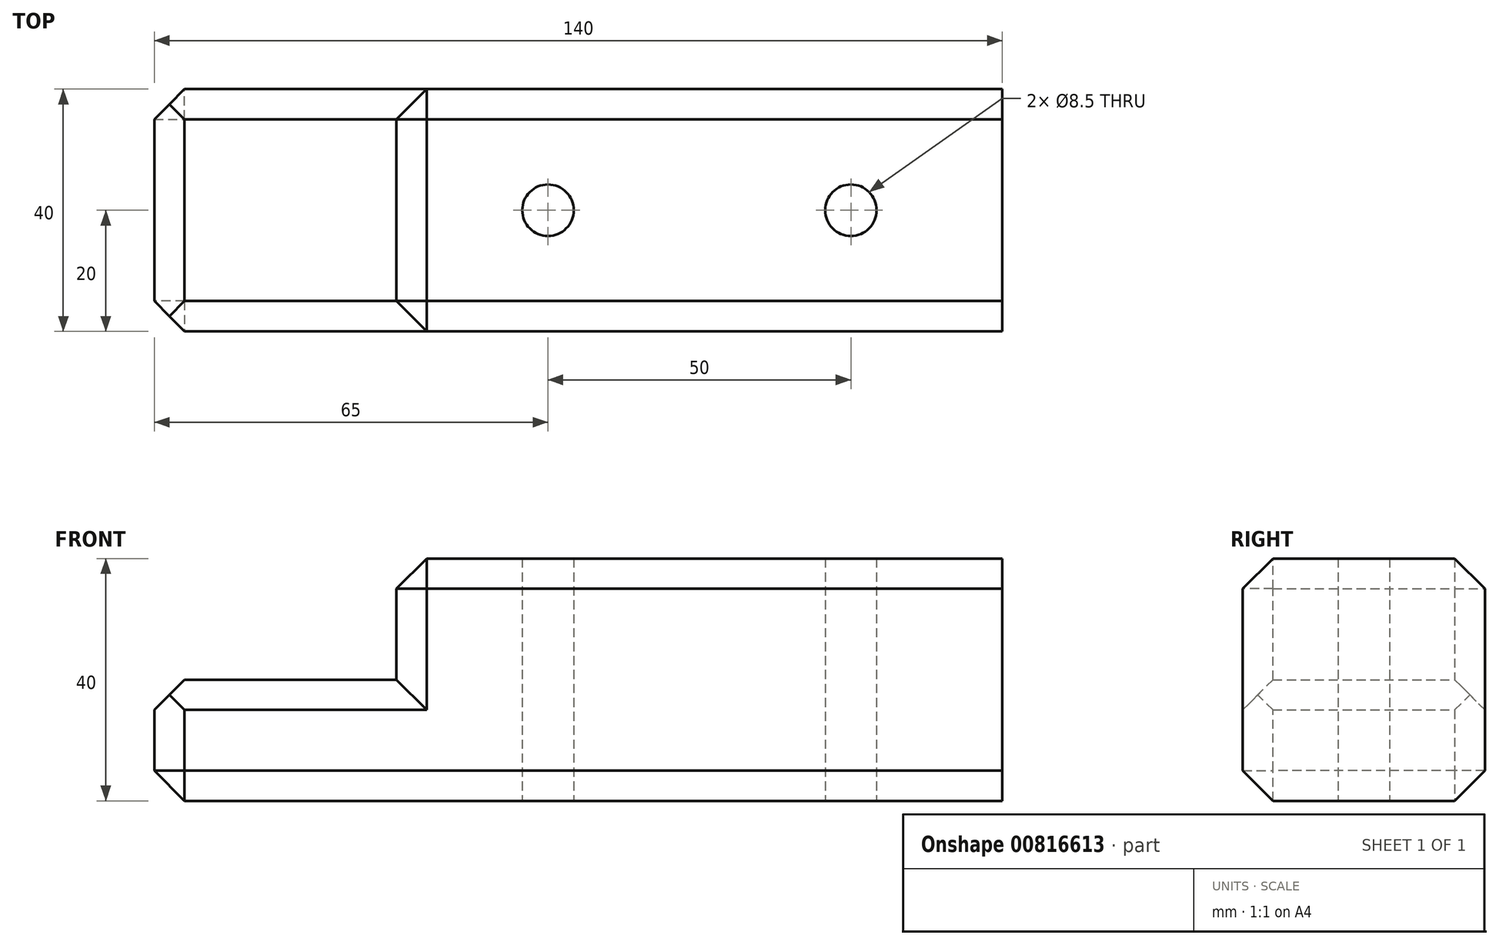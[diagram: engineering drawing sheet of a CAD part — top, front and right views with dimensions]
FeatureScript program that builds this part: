
annotation { "Feature Type Name" : "Feature", "Feature Type Description" : "" }
export const myFeature = defineFeature(function(context is Context, id is Id, definition is map)
    precondition{}
    {
        {
            var Q0;
            Q0=qCreatedBy(makeId("Front.planeOp"),FACE);
            var sketch = newSketch(context, id + "F0", { "sketchPlane" : qUnion([Q0])});
            skLineSegment(sketch, "E0", {"start": v(0, 0) * mm, "end": v(140, 0) * mm});
            skLineSegment(sketch, "E1", {"start": v(140, 0) * mm, "end": v(140, 40) * mm});
            skLineSegment(sketch, "E2", {"start": v(140, 40) * mm, "end": v(40, 40) * mm});
            skLineSegment(sketch, "E3", {"start": v(40, 40) * mm, "end": v(40, 20) * mm});
            skLineSegment(sketch, "E4", {"start": v(40, 20) * mm, "end": v(0, 20) * mm});
            skLineSegment(sketch, "E5", {"start": v(0, 20) * mm, "end": v(0, 0) * mm});
            skSolve(sketch);
        }
        {
            var Q0;
            Q0=makeQuery(id+"F0.imprint","IMPRINT",FACE,{"disambiguationData":[TD([[makeQuery(id+"F0.imprint","IMPRINT",EDGE,{"derivedFrom":sQuery(id+"F0.wireOp",EDGE,"E0")}),1.0]])]});
            extrude(context, id + "F1", {"entities" : qUnion([Q0]), "depth" : 40 * mm, "offsetDistance" : 25 * mm});
        }
        {
            var Q0;
            Q0=makeQuery(id+"F1.opExtrude","SWEPT_EDGE",EDGE,{"disambiguationData":[OSD([sQuery(id+"F0.wireOp",EDGE,"E2"),sQuery(id+"F0.wireOp",EDGE,"E3")])]});
            var Q1;
            Q1=makeQuery(id+"F1.opExtrude","CAP_EDGE",EDGE,{"disambiguationData":[OSD([sQuery(id+"F0.wireOp",EDGE,"E3")])],"isStart":false});
            var Q2;
            Q2=makeQuery(id+"F1.opExtrude","CAP_EDGE",EDGE,{"disambiguationData":[OSD([sQuery(id+"F0.wireOp",EDGE,"E3")])],"isStart":true});
            var Q3;
            Q3=makeQuery(id+"F1.opExtrude","SWEPT_EDGE",EDGE,{"disambiguationData":[OSD([sQuery(id+"F0.wireOp",EDGE,"E4"),sQuery(id+"F0.wireOp",EDGE,"E5")])]});
            var Q4;
            Q4=makeQuery(id+"F1.opExtrude","CAP_EDGE",EDGE,{"disambiguationData":[OSD([sQuery(id+"F0.wireOp",EDGE,"E5")])],"isStart":false});
            var Q5;
            Q5=makeQuery(id+"F1.opExtrude","SWEPT_EDGE",EDGE,{"disambiguationData":[OSD([sQuery(id+"F0.wireOp",EDGE,"E0"),sQuery(id+"F0.wireOp",EDGE,"E5")])]});
            var Q6;
            Q6=makeQuery(id+"F1.opExtrude","CAP_EDGE",EDGE,{"disambiguationData":[OSD([sQuery(id+"F0.wireOp",EDGE,"E5")])],"isStart":true});
            var Q7;
            Q7=makeQuery(id+"F1.opExtrude","CAP_EDGE",EDGE,{"disambiguationData":[OSD([sQuery(id+"F0.wireOp",EDGE,"E2")])],"isStart":false});
            var Q8;
            Q8=makeQuery(id+"F1.opExtrude","CAP_EDGE",EDGE,{"disambiguationData":[OSD([sQuery(id+"F0.wireOp",EDGE,"E0")])],"isStart":false});
            var Q9;
            Q9=makeQuery(id+"F1.opExtrude","CAP_EDGE",EDGE,{"disambiguationData":[OSD([sQuery(id+"F0.wireOp",EDGE,"E2")])],"isStart":true});
            var Q10;
            Q10=makeQuery(id+"F1.opExtrude","CAP_EDGE",EDGE,{"disambiguationData":[OSD([sQuery(id+"F0.wireOp",EDGE,"E0")])],"isStart":true});
            chamfer(context, id + "F2", {"entities" : qUnion([Q0, Q1, Q2, Q3, Q4, Q5, Q6, Q7, Q8, Q9, Q10]), "width" : 5 * mm, "tangentPropagation" : true});
        }
        {
            var Q0;
            Q0=makeQuery(id+"F1.opExtrude","SWEPT_FACE",FACE,{"disambiguationData":[OSD([sQuery(id+"F0.wireOp",EDGE,"E0")])]});
            var sketch = newSketch(context, id + "F3", { "sketchPlane" : qUnion([Q0])});
            skPoint(sketch, "E6", {"position": v(115, 20) * mm});
            skPoint(sketch, "E6.positionSnap0", {"position": v(140, 20) * mm});
            skSolve(sketch);
        }
        {
            var Q0;
            Q0=sQuery(id+"F3.wireOp",VERTEX,"E6");
            var Q1;
            Q1=makeQuery(id+"F1.opExtrude","SWEPT_BODY",BODY,{"disambiguationData":[OSD([sQuery(id+"F0.wireOp",EDGE,"E0"),sQuery(id+"F0.wireOp",EDGE,"E1"),sQuery(id+"F0.wireOp",EDGE,"E2"),sQuery(id+"F0.wireOp",EDGE,"E3"),sQuery(id+"F0.wireOp",EDGE,"E4"),sQuery(id+"F0.wireOp",EDGE,"E5")])]});
            hole(context, id + "F4", {"style" : HoleStyle.SIMPLE, "endStyle" : HoleEndStyle.THROUGH, "standardTappedOrClearance" : lookupTablePath({ "standard" : "ISO", "engagement" : "75%", "pitch" : "1.5 mm", "size" : "M10", "type" : "Tapped" }), "standardBlindInLast" : lookupTablePath({ "standard" : "ISO", "engagement" : "75%", "pitch" : "1.5 mm", "size" : "M10", "type" : "Tapped" }), "holeDiameter" : 8.5 * mm, "majorDiameter" : 10 * mm, "showTappedDepth" : true, "isTappedThrough" : true, "tappedDepth" : 12 * mm, "tapClearance" : 3, "startFromSketch" : true, "locations" : qUnion([Q0]), "scope" : qUnion([Q1])});
        }
        {
            var Q0;
            Q0=makeQuery(id+"F1.opExtrude","SWEPT_FACE",FACE,{"disambiguationData":[OSD([sQuery(id+"F0.wireOp",EDGE,"E0")])]});
            var sketch = newSketch(context, id + "F5", { "sketchPlane" : qUnion([Q0])});
            skPoint(sketch, "E7", {"position": v(65, 20) * mm});
            skPoint(sketch, "E7.positionSnap0", {"position": v(140, 20) * mm});
            skSolve(sketch);
        }
        {
            var Q0;
            Q0=sQuery(id+"F5.wireOp",VERTEX,"E7");
            var Q1;
            Q1=makeQuery(id+"F1.opExtrude","SWEPT_BODY",BODY,{"disambiguationData":[OSD([sQuery(id+"F0.wireOp",EDGE,"E0"),sQuery(id+"F0.wireOp",EDGE,"E1"),sQuery(id+"F0.wireOp",EDGE,"E2"),sQuery(id+"F0.wireOp",EDGE,"E3"),sQuery(id+"F0.wireOp",EDGE,"E4"),sQuery(id+"F0.wireOp",EDGE,"E5")])]});
            hole(context, id + "F6", {"style" : HoleStyle.SIMPLE, "endStyle" : HoleEndStyle.THROUGH, "standardTappedOrClearance" : lookupTablePath({ "standard" : "ISO", "engagement" : "75%", "pitch" : "1.5 mm", "size" : "M10", "type" : "Tapped" }), "standardBlindInLast" : lookupTablePath({ "standard" : "ISO", "engagement" : "75%", "pitch" : "1.5 mm", "size" : "M10", "type" : "Tapped" }), "holeDiameter" : 8.5 * mm, "majorDiameter" : 10 * mm, "showTappedDepth" : true, "isTappedThrough" : true, "tappedDepth" : 12 * mm, "tapClearance" : 3, "startFromSketch" : true, "locations" : qUnion([Q0]), "scope" : qUnion([Q1])});
        }
        {
            var Q0;
            Q0=makeQuery(id+"F1.opExtrude","CAP_EDGE",EDGE,{"disambiguationData":[OSD([sQuery(id+"F0.wireOp",EDGE,"E4")])],"isStart":true});
            chamfer(context, id + "F7", {"entities" : qUnion([Q0]), "width" : 5 * mm, "tangentPropagation" : true});
        }
        {
            var Q0;
            Q0=makeQuery(id+"F1.opExtrude","CAP_EDGE",EDGE,{"disambiguationData":[OSD([sQuery(id+"F0.wireOp",EDGE,"E4")])],"isStart":false});
            chamfer(context, id + "F8", {"entities" : qUnion([Q0]), "width" : 5 * mm, "tangentPropagation" : true});
        }
    });
